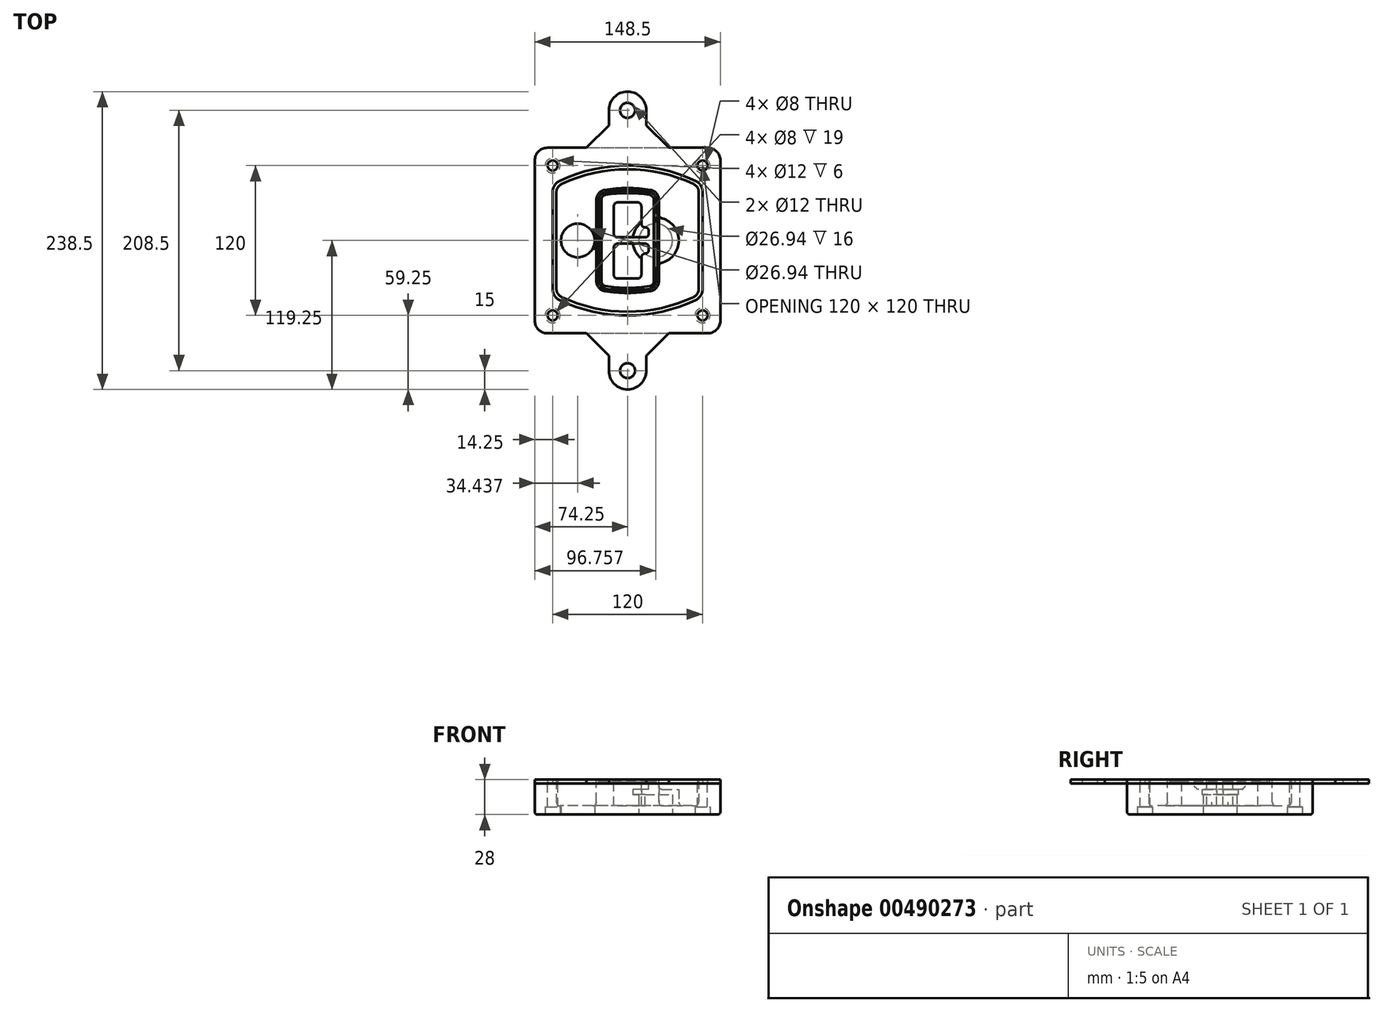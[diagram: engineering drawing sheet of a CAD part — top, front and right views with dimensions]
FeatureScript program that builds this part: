
annotation { "Feature Type Name" : "Feature", "Feature Type Description" : "" }
export const myFeature = defineFeature(function(context is Context, id is Id, definition is map)
    precondition{}
    {
        {
            var Q0;
            Q0=qCreatedBy(makeId("Top.planeOp"),FACE);
            var sketch = newSketch(context, id + "F0", { "sketchPlane" : qUnion([Q0])});
            skPoint(sketch, "E0.rect.middle", {"position": v(0, 0) * mm});
            skLineSegment(sketch, "E1.bottom", {"start": v(-64.25, -74.25) * mm, "end": v(64.25, -74.25) * mm});
            skLineSegment(sketch, "E1.top", {"start": v(-64.25, 74.25) * mm, "end": v(64.25, 74.25) * mm});
            skLineSegment(sketch, "E1.left", {"start": v(-74.25, -64.25) * mm, "end": v(-74.25, 64.25) * mm});
            skLineSegment(sketch, "E1.right", {"start": v(74.25, -64.25) * mm, "end": v(74.25, 64.25) * mm});
            skLineSegment(sketch, "E2", {"start": v(-74.25, 74.25) * mm, "end": v(74.25, -74.25) * mm, "construction": true});
            skLineSegment(sketch, "E3", {"start": v(74.25, 74.25) * mm, "end": v(-74.25, -74.25) * mm, "construction": true});
            skCircle(sketch, "E4", {"center": v(-60, 60) * mm, "radius": 4 * mm});
            skCircle(sketch, "E5", {"center": v(60, 60) * mm, "radius": 4 * mm});
            skCircle(sketch, "E6", {"center": v(60, -60) * mm, "radius": 4 * mm});
            skCircle(sketch, "E7", {"center": v(-60, -60) * mm, "radius": 4 * mm});
            skLineSegment(sketch, "E8", {"start": v(-60, 60) * mm, "end": v(60, 60) * mm, "construction": true});
            skLineSegment(sketch, "E9", {"start": v(60, 60) * mm, "end": v(60, -60) * mm, "construction": true});
            skLineSegment(sketch, "E10", {"start": v(60, -60) * mm, "end": v(-60, -60) * mm, "construction": true});
            skLineSegment(sketch, "E11", {"start": v(-60, -60) * mm, "end": v(-60, 60) * mm, "construction": true});
            skLineSegment(sketch, "E12", {"start": v(-60, 38.83) * mm, "end": v(-60, -38.83) * mm});
            skLineSegment(sketch, "E13", {"start": v(60, 38.83) * mm, "end": v(60, -38.83) * mm});
            skArc(sketch, "E14", {"start": v(54.26, 47.88) * mm, "mid": v(0, 60) * mm, "end": v(-54.26, 47.88) * mm});
            skArc(sketch, "E15", {"start": v(-54.26, -47.88) * mm, "mid": v(0, -60) * mm, "end": v(54.26, -47.88) * mm});
            skLineSegment(sketch, "E16", {"start": v(-60, 0) * mm, "end": v(60, 0) * mm, "construction": true});
            skPoint(sketch, "E17.visualSharp", {"position": v(-60, -45) * mm});
            skArc(sketch, "E17.filletArc", {"start": v(-60, -38.83) * mm, "mid": v(-58.44, -44.2) * mm, "end": v(-54.26, -47.88) * mm});
            skPoint(sketch, "E18.visualSharp", {"position": v(-60, 45) * mm});
            skArc(sketch, "E18.filletArc", {"start": v(-54.26, 47.88) * mm, "mid": v(-58.44, 44.2) * mm, "end": v(-60, 38.83) * mm});
            skPoint(sketch, "E19.visualSharp", {"position": v(60, 45) * mm});
            skArc(sketch, "E19.filletArc", {"start": v(60, 38.83) * mm, "mid": v(58.44, 44.2) * mm, "end": v(54.26, 47.88) * mm});
            skPoint(sketch, "E20.visualSharp", {"position": v(60, -45) * mm});
            skArc(sketch, "E20.filletArc", {"start": v(54.26, -47.88) * mm, "mid": v(58.44, -44.2) * mm, "end": v(60, -38.83) * mm});
            skPoint(sketch, "E21.visualSharp", {"position": v(-74.25, 74.25) * mm});
            skArc(sketch, "E21.filletArc", {"start": v(-64.25, 74.25) * mm, "mid": v(-71.32, 71.32) * mm, "end": v(-74.25, 64.25) * mm});
            skPoint(sketch, "E22.visualSharp", {"position": v(74.25, 74.25) * mm});
            skArc(sketch, "E22.filletArc", {"start": v(74.25, 64.25) * mm, "mid": v(71.32, 71.32) * mm, "end": v(64.25, 74.25) * mm});
            skPoint(sketch, "E23.visualSharp", {"position": v(74.25, -74.25) * mm});
            skArc(sketch, "E23.filletArc", {"start": v(64.25, -74.25) * mm, "mid": v(71.32, -71.32) * mm, "end": v(74.25, -64.25) * mm});
            skPoint(sketch, "E24.visualSharp", {"position": v(-74.25, -74.25) * mm});
            skArc(sketch, "E24.filletArc", {"start": v(-74.25, -64.25) * mm, "mid": v(-71.32, -71.32) * mm, "end": v(-64.25, -74.25) * mm});
            skArc(sketch, "E25.0", {"start": v(57, 38.83) * mm, "mid": v(55.9, 42.58) * mm, "end": v(52.98, 45.17) * mm});
            skLineSegment(sketch, "E25.1", {"start": v(57, 38.83) * mm, "end": v(57, -38.83) * mm});
            skArc(sketch, "E25.2", {"start": v(52.98, -45.17) * mm, "mid": v(55.9, -42.58) * mm, "end": v(57, -38.83) * mm});
            skArc(sketch, "E25.3", {"start": v(-52.98, -45.17) * mm, "mid": v(0, -57) * mm, "end": v(52.98, -45.17) * mm});
            skArc(sketch, "E25.4", {"start": v(-57, -38.83) * mm, "mid": v(-55.9, -42.58) * mm, "end": v(-52.98, -45.17) * mm});
            skArc(sketch, "E25.5", {"start": v(52.98, 45.17) * mm, "mid": v(0, 57) * mm, "end": v(-52.98, 45.17) * mm});
            skLineSegment(sketch, "E25.6", {"start": v(-57, 38.83) * mm, "end": v(-57, -38.83) * mm});
            skArc(sketch, "E25.7", {"start": v(-52.98, 45.17) * mm, "mid": v(-55.9, 42.58) * mm, "end": v(-57, 38.83) * mm});
            skArc(sketch, "E26.0", {"start": v(-55.96, 51.5) * mm, "mid": v(-61.82, 46.33) * mm, "end": v(-64, 38.83) * mm});
            skArc(sketch, "E26.1", {"start": v(55.96, 51.5) * mm, "mid": v(0, 64) * mm, "end": v(-55.96, 51.5) * mm});
            skArc(sketch, "E26.2", {"start": v(64, 38.83) * mm, "mid": v(61.82, 46.33) * mm, "end": v(55.96, 51.5) * mm});
            skLineSegment(sketch, "E26.3", {"start": v(64, 38.83) * mm, "end": v(64, -38.83) * mm});
            skArc(sketch, "E26.4", {"start": v(55.96, -51.5) * mm, "mid": v(61.82, -46.33) * mm, "end": v(64, -38.83) * mm});
            skLineSegment(sketch, "E26.5", {"start": v(-64, 38.83) * mm, "end": v(-64, -38.83) * mm});
            skArc(sketch, "E26.6", {"start": v(-55.96, -51.5) * mm, "mid": v(0, -64) * mm, "end": v(55.96, -51.5) * mm});
            skArc(sketch, "E26.7", {"start": v(-64, -38.83) * mm, "mid": v(-61.82, -46.33) * mm, "end": v(-55.96, -51.5) * mm});
            skSolve(sketch);
        }
        {
            var Q0;
            Q0=makeQuery(id+"F0.imprint","IMPRINT",FACE,{"disambiguationData":[TD([[makeQuery(id+"F0.imprint","IMPRINT",EDGE,{"derivedFrom":sQuery(id+"F0.wireOp",EDGE,"E1.bottom")}),1.0]])]});
            var Q1;
            Q1=makeQuery(id+"F0.imprint","IMPRINT",FACE,{"disambiguationData":[TD([[makeQuery(id+"F0.imprint","IMPRINT",EDGE,{"derivedFrom":sQuery(id+"F0.wireOp",EDGE,"E12")}),1.0]])]});
            var Q2;
            Q2=makeQuery(id+"F0.imprint","IMPRINT",FACE,{"disambiguationData":[TD([[makeQuery(id+"F0.imprint","IMPRINT",EDGE,{"derivedFrom":sQuery(id+"F0.wireOp",EDGE,"E25.0")}),1.0]])]});
            var Q3;
            Q3=makeQuery(id+"F0.imprint","IMPRINT",FACE,{"disambiguationData":[TD([[makeQuery(id+"F0.imprint","IMPRINT",EDGE,{"derivedFrom":sQuery(id+"F0.wireOp",EDGE,"E12")}),-1.0]])]});
            extrude(context, id + "F1", {"entities" : qUnion([Q0, Q1, Q2, Q3]), "oppositeDirection" : true, "depth" : 25 * mm});
        }
        {
            var Q0;
            Q0=makeQuery(id+"F0.imprint","IMPRINT",FACE,{"disambiguationData":[TD([[makeQuery(id+"F0.imprint","IMPRINT",EDGE,{"derivedFrom":sQuery(id+"F0.wireOp",EDGE,"E12")}),1.0]])]});
            extrude(context, id + "F2", {"entities" : qUnion([Q0]), "operationType" : NewBodyOperationType.ADD, "depth" : 3 * mm});
        }
        {
            var Q0;
            Q0=makeQuery(id+"F0.imprint","IMPRINT",FACE,{"disambiguationData":[TD([[makeQuery(id+"F0.imprint","IMPRINT",EDGE,{"derivedFrom":sQuery(id+"F0.wireOp",EDGE,"E25.0")}),1.0]])]});
            extrude(context, id + "F3", {"entities" : qUnion([Q0]), "operationType" : NewBodyOperationType.REMOVE, "oppositeDirection" : true, "depth" : 18 * mm});
        }
        {
            var Q0;
            Q0=makeQuery(id+"F2.opExtrude","CAP_FACE",FACE,{"disambiguationData":[OSD([sQuery(id+"F0.wireOp",EDGE,"E12"),sQuery(id+"F0.wireOp",EDGE,"E13"),sQuery(id+"F0.wireOp",EDGE,"E14"),sQuery(id+"F0.wireOp",EDGE,"E15"),sQuery(id+"F0.wireOp",EDGE,"E17.filletArc"),sQuery(id+"F0.wireOp",EDGE,"E18.filletArc"),sQuery(id+"F0.wireOp",EDGE,"E19.filletArc"),sQuery(id+"F0.wireOp",EDGE,"E20.filletArc"),sQuery(id+"F0.wireOp",EDGE,"E25.0"),sQuery(id+"F0.wireOp",EDGE,"E25.1"),sQuery(id+"F0.wireOp",EDGE,"E25.2"),sQuery(id+"F0.wireOp",EDGE,"E25.3"),sQuery(id+"F0.wireOp",EDGE,"E25.4"),sQuery(id+"F0.wireOp",EDGE,"E25.5"),sQuery(id+"F0.wireOp",EDGE,"E25.6"),sQuery(id+"F0.wireOp",EDGE,"E25.7")])],"isStart":false});
            var sketch = newSketch(context, id + "F4", { "sketchPlane" : qUnion([Q0])});
            skArc(sketch, "E27.0", {"start": v(-18.34, -40.45) * mm, "mid": v(0, -42) * mm, "end": v(18.34, -40.45) * mm});
            skArc(sketch, "E28.0", {"start": v(18.34, 40.45) * mm, "mid": v(0, 42) * mm, "end": v(-18.34, 40.45) * mm});
            skLineSegment(sketch, "E29", {"start": v(-25, 32.57) * mm, "end": v(-25, -32.57) * mm});
            skLineSegment(sketch, "E30", {"start": v(25, 32.57) * mm, "end": v(25, -32.57) * mm});
            skLineSegment(sketch, "E31", {"start": v(-25, 39.1) * mm, "end": v(25, 39.1) * mm, "construction": true});
            skLineSegment(sketch, "E32", {"start": v(-25, -39.1) * mm, "end": v(25, -39.1) * mm, "construction": true});
            skPoint(sketch, "E33.visualSharp", {"position": v(-25, 39.1) * mm});
            skArc(sketch, "E33.filletArc", {"start": v(-18.34, 40.45) * mm, "mid": v(-23.11, 37.73) * mm, "end": v(-25, 32.57) * mm});
            skPoint(sketch, "E34.visualSharp", {"position": v(25, 39.1) * mm});
            skArc(sketch, "E34.filletArc", {"start": v(25, 32.57) * mm, "mid": v(23.11, 37.73) * mm, "end": v(18.34, 40.45) * mm});
            skPoint(sketch, "E35.visualSharp", {"position": v(25, -39.1) * mm});
            skArc(sketch, "E35.filletArc", {"start": v(18.34, -40.45) * mm, "mid": v(23.11, -37.73) * mm, "end": v(25, -32.57) * mm});
            skPoint(sketch, "E36.visualSharp", {"position": v(-25, -39.1) * mm});
            skArc(sketch, "E36.filletArc", {"start": v(-25, -32.57) * mm, "mid": v(-23.11, -37.73) * mm, "end": v(-18.34, -40.45) * mm});
            skArc(sketch, "E37.0", {"start": v(52.98, 45.17) * mm, "mid": v(0, 57) * mm, "end": v(-52.98, 45.17) * mm});
            skArc(sketch, "E37.1", {"start": v(-52.98, 45.17) * mm, "mid": v(-55.9, 42.58) * mm, "end": v(-57, 38.83) * mm});
            skLineSegment(sketch, "E37.2", {"start": v(-57, 38.83) * mm, "end": v(-57, -38.83) * mm});
            skArc(sketch, "E37.3", {"start": v(-57, -38.83) * mm, "mid": v(-55.9, -42.58) * mm, "end": v(-52.98, -45.17) * mm});
            skArc(sketch, "E37.4", {"start": v(-52.98, -45.17) * mm, "mid": v(0, -57) * mm, "end": v(52.98, -45.17) * mm});
            skArc(sketch, "E37.5", {"start": v(52.98, -45.17) * mm, "mid": v(55.9, -42.58) * mm, "end": v(57, -38.83) * mm});
            skLineSegment(sketch, "E37.6", {"start": v(57, 38.83) * mm, "end": v(57, -38.83) * mm});
            skArc(sketch, "E37.7", {"start": v(57, 38.83) * mm, "mid": v(55.9, 42.58) * mm, "end": v(52.98, 45.17) * mm});
            skLineSegment(sketch, "E38.0", {"start": v(23, 32.57) * mm, "end": v(23, -32.57) * mm});
            skArc(sketch, "E38.1", {"start": v(18, -38.48) * mm, "mid": v(21.58, -36.44) * mm, "end": v(23, -32.57) * mm});
            skArc(sketch, "E38.2", {"start": v(-18, -38.48) * mm, "mid": v(0, -40) * mm, "end": v(18, -38.48) * mm});
            skArc(sketch, "E38.3", {"start": v(-23, -32.57) * mm, "mid": v(-21.58, -36.44) * mm, "end": v(-18, -38.48) * mm});
            skLineSegment(sketch, "E38.4", {"start": v(-23, 32.57) * mm, "end": v(-23, -32.57) * mm});
            skArc(sketch, "E38.5", {"start": v(23, 32.57) * mm, "mid": v(21.58, 36.44) * mm, "end": v(18, 38.48) * mm});
            skArc(sketch, "E38.6", {"start": v(-18, 38.48) * mm, "mid": v(-21.58, 36.44) * mm, "end": v(-23, 32.57) * mm});
            skArc(sketch, "E38.7", {"start": v(18, 38.48) * mm, "mid": v(0, 40) * mm, "end": v(-18, 38.48) * mm});
            skArc(sketch, "E39.0", {"start": v(21, 32.57) * mm, "mid": v(20.06, 35.15) * mm, "end": v(17.67, 36.5) * mm});
            skLineSegment(sketch, "E39.1", {"start": v(21, 32.57) * mm, "end": v(21, -32.57) * mm});
            skArc(sketch, "E39.2", {"start": v(17.67, -36.5) * mm, "mid": v(20.06, -35.15) * mm, "end": v(21, -32.57) * mm});
            skArc(sketch, "E39.3", {"start": v(-17.67, -36.5) * mm, "mid": v(0, -38) * mm, "end": v(17.67, -36.5) * mm});
            skArc(sketch, "E39.4", {"start": v(-21, -32.57) * mm, "mid": v(-20.06, -35.15) * mm, "end": v(-17.67, -36.5) * mm});
            skArc(sketch, "E39.5", {"start": v(17.67, 36.5) * mm, "mid": v(0, 38) * mm, "end": v(-17.67, 36.5) * mm});
            skLineSegment(sketch, "E39.6", {"start": v(-21, 32.57) * mm, "end": v(-21, -32.57) * mm});
            skArc(sketch, "E39.7", {"start": v(-17.67, 36.5) * mm, "mid": v(-20.06, 35.15) * mm, "end": v(-21, 32.57) * mm});
            skLineSegment(sketch, "E40", {"start": v(-25, 0) * mm, "end": v(25, 0) * mm, "construction": true});
            skLineSegment(sketch, "E41", {"start": v(-11, 5.5) * mm, "end": v(-11, 27.5) * mm});
            skLineSegment(sketch, "E42", {"start": v(-8, 30.5) * mm, "end": v(8, 30.5) * mm});
            skLineSegment(sketch, "E43", {"start": v(11, 27.5) * mm, "end": v(11, 13.5) * mm});
            skLineSegment(sketch, "E44", {"start": v(14, 10.5) * mm, "end": v(14, 10.5) * mm});
            skLineSegment(sketch, "E45", {"start": v(17, 7.5) * mm, "end": v(17, 5.5) * mm});
            skLineSegment(sketch, "E46", {"start": v(14, 2.5) * mm, "end": v(-8, 2.5) * mm});
            skPoint(sketch, "E47.visualSharp", {"position": v(-11, 30.5) * mm});
            skArc(sketch, "E47.filletArc", {"start": v(-8, 30.5) * mm, "mid": v(-10.12, 29.62) * mm, "end": v(-11, 27.5) * mm});
            skPoint(sketch, "E48.visualSharp", {"position": v(11, 30.5) * mm});
            skArc(sketch, "E48.filletArc", {"start": v(11, 27.5) * mm, "mid": v(10.12, 29.62) * mm, "end": v(8, 30.5) * mm});
            skPoint(sketch, "E49.visualSharp", {"position": v(11, 10.5) * mm});
            skArc(sketch, "E49.filletArc", {"start": v(11, 13.5) * mm, "mid": v(11.88, 11.38) * mm, "end": v(14, 10.5) * mm});
            skPoint(sketch, "E50.visualSharp", {"position": v(17, 10.5) * mm});
            skArc(sketch, "E50.filletArc", {"start": v(17, 7.5) * mm, "mid": v(16.12, 9.62) * mm, "end": v(14, 10.5) * mm});
            skPoint(sketch, "E51.visualSharp", {"position": v(17, 2.5) * mm});
            skArc(sketch, "E51.filletArc", {"start": v(14, 2.5) * mm, "mid": v(16.12, 3.38) * mm, "end": v(17, 5.5) * mm});
            skPoint(sketch, "E52.visualSharp", {"position": v(-11, 2.5) * mm});
            skArc(sketch, "E52.filletArc", {"start": v(-11, 5.5) * mm, "mid": v(-10.12, 3.38) * mm, "end": v(-8, 2.5) * mm});
            skLineSegment(sketch, "E53.0.MirrorCS", {"start": v(14, -2.5) * mm, "end": v(-8, -2.5) * mm});
            skArc(sketch, "E54.0.MirrorCS", {"start": v(-11, -5.5) * mm, "mid": v(-10.12, -3.38) * mm, "end": v(-8, -2.5) * mm});
            skLineSegment(sketch, "E55.0.MirrorCS", {"start": v(-11, -5.5) * mm, "end": v(-11, -27.5) * mm});
            skArc(sketch, "E56.0.MirrorCS", {"start": v(-8, -30.5) * mm, "mid": v(-10.12, -29.62) * mm, "end": v(-11, -27.5) * mm});
            skLineSegment(sketch, "E57.0.MirrorCS", {"start": v(-8, -30.5) * mm, "end": v(8, -30.5) * mm});
            skArc(sketch, "E58.0.MirrorCS", {"start": v(11, -27.5) * mm, "mid": v(10.12, -29.62) * mm, "end": v(8, -30.5) * mm});
            skLineSegment(sketch, "E59.0.MirrorCS", {"start": v(11, -27.5) * mm, "end": v(11, -13.5) * mm});
            skArc(sketch, "E60.0.MirrorCS", {"start": v(11, -13.5) * mm, "mid": v(11.88, -11.38) * mm, "end": v(14, -10.5) * mm});
            skArc(sketch, "E61.0.MirrorCS", {"start": v(17, -7.5) * mm, "mid": v(16.12, -9.62) * mm, "end": v(14, -10.5) * mm});
            skLineSegment(sketch, "E62.0.MirrorCS", {"start": v(17, -7.5) * mm, "end": v(17, -5.5) * mm});
            skArc(sketch, "E63.0.MirrorCS", {"start": v(14, -2.5) * mm, "mid": v(16.12, -3.38) * mm, "end": v(17, -5.5) * mm});
            skSolve(sketch);
        }
        {
            var Q0;
            Q0=makeQuery(id+"F4.imprint","IMPRINT",FACE,{"disambiguationData":[TD([[makeQuery(id+"F4.imprint","IMPRINT",EDGE,{"derivedFrom":sQuery(id+"F4.wireOp",EDGE,"E27.0")}),1.0]])]});
            var Q1;
            Q1=makeQuery(id+"F4.imprint","IMPRINT",FACE,{"disambiguationData":[TD([[makeQuery(id+"F4.imprint","IMPRINT",EDGE,{"derivedFrom":sQuery(id+"F4.wireOp",EDGE,"E38.0")}),-1.0]])]});
            var Q2;
            Q2=makeQuery(id+"F4.imprint","IMPRINT",FACE,{"disambiguationData":[TD([[makeQuery(id+"F4.imprint","IMPRINT",EDGE,{"derivedFrom":sQuery(id+"F4.wireOp",EDGE,"E39.0")}),1.0]])]});
            extrude(context, id + "F5", {"entities" : qUnion([Q0, Q1, Q2]), "operationType" : NewBodyOperationType.ADD, "endBound" : BoundingType.UP_TO_NEXT, "oppositeDirection" : true, "depth" : 25 * mm});
        }
        {
            var Q0;
            Q0=makeQuery(id+"F4.imprint","IMPRINT",FACE,{"disambiguationData":[TD([[makeQuery(id+"F4.imprint","IMPRINT",EDGE,{"derivedFrom":sQuery(id+"F4.wireOp",EDGE,"E38.0")}),-1.0]])]});
            extrude(context, id + "F6", {"entities" : qUnion([Q0]), "operationType" : NewBodyOperationType.REMOVE, "oppositeDirection" : true, "depth" : 2 * mm});
        }
        {
            var Q0;
            Q0=makeQuery(id+"F1.opExtrude","CAP_FACE",FACE,{"disambiguationData":[OSD([sQuery(id+"F0.wireOp",EDGE,"E1.bottom"),sQuery(id+"F0.wireOp",EDGE,"E1.top"),sQuery(id+"F0.wireOp",EDGE,"E1.left"),sQuery(id+"F0.wireOp",EDGE,"E1.right"),sQuery(id+"F0.wireOp",EDGE,"E4"),sQuery(id+"F0.wireOp",EDGE,"E5"),sQuery(id+"F0.wireOp",EDGE,"E6"),sQuery(id+"F0.wireOp",EDGE,"E7"),sQuery(id+"F0.wireOp",EDGE,"E21.filletArc"),sQuery(id+"F0.wireOp",EDGE,"E22.filletArc"),sQuery(id+"F0.wireOp",EDGE,"E23.filletArc"),sQuery(id+"F0.wireOp",EDGE,"E24.filletArc")])],"isStart":false});
            var sketch = newSketch(context, id + "F7", { "sketchPlane" : qUnion([Q0])});
            skCircle(sketch, "E64", {"center": v(22.5, 0) * mm, "radius": 13.47 * mm});
            skCircle(sketch, "E65", {"center": v(-39.81, 0) * mm, "radius": 13.47 * mm});
            skLineSegment(sketch, "E66", {"start": v(74.25, 0) * mm, "end": v(-74.25, 0) * mm});
            skCircle(sketch, "E67", {"center": v(22.5, 0) * mm, "radius": 18.47 * mm});
            skCircle(sketch, "E68", {"center": v(60, -60) * mm, "radius": 6 * mm});
            skCircle(sketch, "E69", {"center": v(-60, -60) * mm, "radius": 6 * mm});
            skCircle(sketch, "E70", {"center": v(-60, 60) * mm, "radius": 6 * mm});
            skCircle(sketch, "E71", {"center": v(60, 60) * mm, "radius": 6 * mm});
            skSolve(sketch);
        }
        {
            var Q0;
            {var subQ1=sQuery(id+"F7.wireOp",EDGE,"E66");var subQ4=sQuery(id+"F7.wireOp",EDGE,"E64");var subQ6=makeQuery(id+"F7.imprint","INTERSECT",VERTEX,{"disambiguationData":[OD(0.0)],"derivedFrom":[subQ4,subQ1]});Q0=makeQuery(id+"F7.imprint","IMPRINT",FACE,{"disambiguationData":[TD([[makeQuery(id+"F7.imprint","IMPRINT",EDGE,{"disambiguationData":[TD([[subQ6,-1.0]])],"derivedFrom":subQ4}),-1.0]])]});}
            var Q1;
            {var subQ0=sQuery(id+"F7.wireOp",EDGE,"E66");var subQ1=sQuery(id+"F7.wireOp",EDGE,"E64");var subQ3=makeQuery(id+"F7.imprint","INTERSECT",VERTEX,{"disambiguationData":[OD(0.0)],"derivedFrom":[subQ1,subQ0]});Q1=makeQuery(id+"F7.imprint","IMPRINT",FACE,{"disambiguationData":[TD([[makeQuery(id+"F7.imprint","IMPRINT",EDGE,{"disambiguationData":[TD([[subQ3,-1.0]])],"derivedFrom":subQ1}),1.0]])]});}
            var Q2;
            {var subQ0=sQuery(id+"F7.wireOp",EDGE,"E66");var subQ1=sQuery(id+"F7.wireOp",EDGE,"E64");var subQ3=makeQuery(id+"F7.imprint","INTERSECT",VERTEX,{"disambiguationData":[OD(0.0)],"derivedFrom":[subQ1,subQ0]});Q2=makeQuery(id+"F7.imprint","IMPRINT",FACE,{"disambiguationData":[TD([[makeQuery(id+"F7.imprint","IMPRINT",EDGE,{"disambiguationData":[TD([[subQ3,1.0]])],"derivedFrom":subQ1}),1.0]])]});}
            var Q3;
            {var subQ1=sQuery(id+"F7.wireOp",EDGE,"E66");var subQ4=sQuery(id+"F7.wireOp",EDGE,"E64");var subQ6=makeQuery(id+"F7.imprint","INTERSECT",VERTEX,{"disambiguationData":[OD(0.0)],"derivedFrom":[subQ4,subQ1]});Q3=makeQuery(id+"F7.imprint","IMPRINT",FACE,{"disambiguationData":[TD([[makeQuery(id+"F7.imprint","IMPRINT",EDGE,{"disambiguationData":[TD([[subQ6,1.0]])],"derivedFrom":subQ4}),-1.0]])]});}
            extrude(context, id + "F8", {"entities" : qUnion([Q0, Q1, Q2, Q3]), "operationType" : NewBodyOperationType.ADD, "oppositeDirection" : true, "depth" : 20 * mm});
        }
        {
            var Q0;
            {var subQ0=sQuery(id+"F7.wireOp",EDGE,"E66");var subQ1=sQuery(id+"F7.wireOp",EDGE,"E64");var subQ3=makeQuery(id+"F7.imprint","INTERSECT",VERTEX,{"disambiguationData":[OD(0.0)],"derivedFrom":[subQ1,subQ0]});Q0=makeQuery(id+"F7.imprint","IMPRINT",FACE,{"disambiguationData":[TD([[makeQuery(id+"F7.imprint","IMPRINT",EDGE,{"disambiguationData":[TD([[subQ3,-1.0]])],"derivedFrom":subQ1}),1.0]])]});}
            var Q1;
            {var subQ0=sQuery(id+"F7.wireOp",EDGE,"E66");var subQ1=sQuery(id+"F7.wireOp",EDGE,"E64");var subQ3=makeQuery(id+"F7.imprint","INTERSECT",VERTEX,{"disambiguationData":[OD(0.0)],"derivedFrom":[subQ1,subQ0]});Q1=makeQuery(id+"F7.imprint","IMPRINT",FACE,{"disambiguationData":[TD([[makeQuery(id+"F7.imprint","IMPRINT",EDGE,{"disambiguationData":[TD([[subQ3,1.0]])],"derivedFrom":subQ1}),1.0]])]});}
            extrude(context, id + "F9", {"entities" : qUnion([Q0, Q1]), "operationType" : NewBodyOperationType.REMOVE, "oppositeDirection" : true, "depth" : 16 * mm});
        }
        {
            var Q0;
            {var subQ0=sQuery(id+"F7.wireOp",EDGE,"E66");var subQ1=sQuery(id+"F7.wireOp",EDGE,"E65");var subQ3=makeQuery(id+"F7.imprint","INTERSECT",VERTEX,{"disambiguationData":[OD(0.0)],"derivedFrom":[subQ1,subQ0]});Q0=makeQuery(id+"F7.imprint","IMPRINT",FACE,{"disambiguationData":[TD([[makeQuery(id+"F7.imprint","IMPRINT",EDGE,{"disambiguationData":[TD([[subQ3,-1.0]])],"derivedFrom":subQ1}),1.0]])]});}
            var Q1;
            {var subQ0=sQuery(id+"F7.wireOp",EDGE,"E66");var subQ1=sQuery(id+"F7.wireOp",EDGE,"E65");var subQ3=makeQuery(id+"F7.imprint","INTERSECT",VERTEX,{"disambiguationData":[OD(0.0)],"derivedFrom":[subQ1,subQ0]});Q1=makeQuery(id+"F7.imprint","IMPRINT",FACE,{"disambiguationData":[TD([[makeQuery(id+"F7.imprint","IMPRINT",EDGE,{"disambiguationData":[TD([[subQ3,1.0]])],"derivedFrom":subQ1}),1.0]])]});}
            extrude(context, id + "F10", {"entities" : qUnion([Q0, Q1]), "operationType" : NewBodyOperationType.REMOVE, "oppositeDirection" : true, "depth" : 25 * mm});
        }
        {
            var Q0;
            Q0=makeQuery(id+"F7.imprint","IMPRINT",FACE,{"disambiguationData":[TD([[makeQuery(id+"F7.imprint","IMPRINT",EDGE,{"derivedFrom":sQuery(id+"F7.wireOp",EDGE,"E68")}),1.0]])]});
            var Q1;
            Q1=makeQuery(id+"F7.imprint","IMPRINT",FACE,{"disambiguationData":[TD([[makeQuery(id+"F7.imprint","IMPRINT",EDGE,{"derivedFrom":makeQuery(id+"F1.opExtrude","CAP_EDGE",EDGE,{"disambiguationData":[OSD([sQuery(id+"F0.wireOp",EDGE,"E5")])],"isStart":false})}),-1.0]])]});
            var Q2;
            Q2=makeQuery(id+"F7.imprint","IMPRINT",FACE,{"disambiguationData":[TD([[makeQuery(id+"F7.imprint","IMPRINT",EDGE,{"derivedFrom":sQuery(id+"F7.wireOp",EDGE,"E69")}),1.0]])]});
            var Q3;
            Q3=makeQuery(id+"F7.imprint","IMPRINT",FACE,{"disambiguationData":[TD([[makeQuery(id+"F7.imprint","IMPRINT",EDGE,{"derivedFrom":makeQuery(id+"F1.opExtrude","CAP_EDGE",EDGE,{"disambiguationData":[OSD([sQuery(id+"F0.wireOp",EDGE,"E4")])],"isStart":false})}),-1.0]])]});
            var Q4;
            Q4=makeQuery(id+"F7.imprint","IMPRINT",FACE,{"disambiguationData":[TD([[makeQuery(id+"F7.imprint","IMPRINT",EDGE,{"derivedFrom":sQuery(id+"F7.wireOp",EDGE,"E70")}),1.0]])]});
            var Q5;
            Q5=makeQuery(id+"F7.imprint","IMPRINT",FACE,{"disambiguationData":[TD([[makeQuery(id+"F7.imprint","IMPRINT",EDGE,{"derivedFrom":makeQuery(id+"F1.opExtrude","CAP_EDGE",EDGE,{"disambiguationData":[OSD([sQuery(id+"F0.wireOp",EDGE,"E7")])],"isStart":false})}),-1.0]])]});
            var Q6;
            Q6=makeQuery(id+"F7.imprint","IMPRINT",FACE,{"disambiguationData":[TD([[makeQuery(id+"F7.imprint","IMPRINT",EDGE,{"derivedFrom":sQuery(id+"F7.wireOp",EDGE,"E71")}),1.0]])]});
            var Q7;
            Q7=makeQuery(id+"F7.imprint","IMPRINT",FACE,{"disambiguationData":[TD([[makeQuery(id+"F7.imprint","IMPRINT",EDGE,{"derivedFrom":makeQuery(id+"F1.opExtrude","CAP_EDGE",EDGE,{"disambiguationData":[OSD([sQuery(id+"F0.wireOp",EDGE,"E6")])],"isStart":false})}),-1.0]])]});
            extrude(context, id + "F11", {"entities" : qUnion([Q0, Q1, Q2, Q3, Q4, Q5, Q6, Q7]), "operationType" : NewBodyOperationType.REMOVE, "oppositeDirection" : true, "depth" : 6 * mm});
        }
        {
            var Q0;
            Q0=makeQuery(id+"F9.boolean.opBoolean","COPY",FACE,{"derivedFrom":makeQuery(id+"F9.opExtrude","CAP_FACE",FACE,{"disambiguationData":[OSD([sQuery(id+"F7.wireOp",EDGE,"E64")])],"isStart":false})});
            var sketch = newSketch(context, id + "F12", { "sketchPlane" : qUnion([Q0])});
            skArc(sketch, "E72.0", {"start": v(11, 14.45) * mm, "mid": v(6.45, 9.13) * mm, "end": v(4.2, 2.5) * mm});
            skArc(sketch, "E72.1", {"start": v(4.2, -2.5) * mm, "mid": v(6.45, -9.13) * mm, "end": v(11, -14.45) * mm});
            skLineSegment(sketch, "E73", {"start": v(4.2, -2.5) * mm, "end": v(14, -2.5) * mm});
            skLineSegment(sketch, "E74.0", {"start": v(14, 2.5) * mm, "end": v(4.2, 2.5) * mm});
            skArc(sketch, "E74.1", {"start": v(14, 2.5) * mm, "mid": v(16.12, 3.38) * mm, "end": v(17, 5.5) * mm});
            skLineSegment(sketch, "E74.2", {"start": v(17, 7.5) * mm, "end": v(17, 5.5) * mm});
            skArc(sketch, "E74.3", {"start": v(17, 7.5) * mm, "mid": v(16.12, 9.62) * mm, "end": v(14, 10.5) * mm});
            skArc(sketch, "E74.4", {"start": v(11, 13.5) * mm, "mid": v(11.88, 11.38) * mm, "end": v(14, 10.5) * mm});
            skLineSegment(sketch, "E74.5", {"start": v(11, 14.45) * mm, "end": v(11, 13.5) * mm});
            skLineSegment(sketch, "E74.7", {"start": v(14, -2.5) * mm, "end": v(4.2, -2.5) * mm});
            skArc(sketch, "E74.8", {"start": v(14, -2.5) * mm, "mid": v(16.12, -3.38) * mm, "end": v(17, -5.5) * mm});
            skLineSegment(sketch, "E74.9", {"start": v(17, -7.5) * mm, "end": v(17, -5.5) * mm});
            skArc(sketch, "E74.10", {"start": v(17, -7.5) * mm, "mid": v(16.12, -9.62) * mm, "end": v(14, -10.5) * mm});
            skArc(sketch, "E74.11", {"start": v(11, -13.5) * mm, "mid": v(11.88, -11.38) * mm, "end": v(14, -10.5) * mm});
            skLineSegment(sketch, "E74.12", {"start": v(11, -14.45) * mm, "end": v(11, -13.5) * mm});
            skPoint(sketch, "E75.orphan", {"position": v(11, -27.5) * mm});
            skPoint(sketch, "E76.orphan", {"position": v(-8, -2.5) * mm});
            skPoint(sketch, "E77.orphan", {"position": v(-8, 2.5) * mm});
            skPoint(sketch, "E78.orphan", {"position": v(11, 27.5) * mm});
            skSolve(sketch);
        }
        {
            var Q0;
            {var subQ7=sQuery(id+"F12.wireOp",EDGE,"E72.0");var subQ14=sQuery(id+"F12.wireOp",EDGE,"E72.1");var subQ16=sQuery(id+"F12.wireOp",EDGE,"E74.1");var subQ18=sQuery(id+"F12.wireOp",EDGE,"E74.8");Q0=qUnion([makeQuery(id+"F12.imprint","IMPRINT",FACE,{"disambiguationData":[TD([[makeQuery(id+"F12.imprint","IMPRINT",EDGE,{"derivedFrom":subQ7}),1.0]])]}),makeQuery(id+"F12.imprint","IMPRINT",FACE,{"disambiguationData":[TD([[makeQuery(id+"F12.imprint","IMPRINT",EDGE,{"derivedFrom":subQ14}),1.0]])]}),makeQuery(id+"F12.imprint","IMPRINT",FACE,{"disambiguationData":[TD([[makeQuery(id+"F12.imprint","IMPRINT",EDGE,{"derivedFrom":subQ16}),1.0]])]}),makeQuery(id+"F12.imprint","IMPRINT",FACE,{"disambiguationData":[TD([[makeQuery(id+"F12.imprint","IMPRINT",EDGE,{"derivedFrom":subQ18}),-1.0]])]})]);}
            var Q1;
            Q1=makeQuery(id+"F5.boolean.opBoolean","SPLIT",FACE,{"disambiguationData":[TD([makeQuery(id+"F5.opExtrude","SWEPT_FACE",FACE,{"disambiguationData":[OSD([sQuery(id+"F4.wireOp",EDGE,"E41")])]})])],"derivedFrom":makeQuery(id+"F3.boolean.opBoolean","COPY",FACE,{"derivedFrom":makeQuery(id+"F3.opExtrude","CAP_FACE",FACE,{"disambiguationData":[OSD([sQuery(id+"F0.wireOp",EDGE,"E25.0"),sQuery(id+"F0.wireOp",EDGE,"E25.1"),sQuery(id+"F0.wireOp",EDGE,"E25.2"),sQuery(id+"F0.wireOp",EDGE,"E25.3"),sQuery(id+"F0.wireOp",EDGE,"E25.4"),sQuery(id+"F0.wireOp",EDGE,"E25.5"),sQuery(id+"F0.wireOp",EDGE,"E25.6"),sQuery(id+"F0.wireOp",EDGE,"E25.7")])],"isStart":false})})});
            extrude(context, id + "F13", {"entities" : qUnion([Q0]), "operationType" : NewBodyOperationType.REMOVE, "endBound" : BoundingType.UP_TO_SURFACE, "endBoundEntityFace" : qUnion([Q1]), "depth" : 25 * mm});
        }
        {
            var Q0;
            Q0=makeQuery(id+"F3.boolean.opBoolean","COPY",EDGE,{"derivedFrom":makeQuery(id+"F3.opExtrude","CAP_EDGE",EDGE,{"disambiguationData":[OSD([sQuery(id+"F0.wireOp",EDGE,"E25.6")])],"isStart":false})});
            var Q1;
            Q1=makeQuery(id+"F8.boolean.opBoolean","INTERSECT",EDGE,{"derivedFrom":[makeQuery(id+"F5.opExtrude","SWEPT_FACE",FACE,{"disambiguationData":[OSD([sQuery(id+"F4.wireOp",EDGE,"E30")])]}),makeQuery(id+"F8.opExtrude","CAP_FACE",FACE,{"disambiguationData":[OSD([sQuery(id+"F7.wireOp",EDGE,"E67")])],"isStart":false})]});
            var Q2;
            Q2=makeQuery(id+"F8.boolean.opBoolean","INTERSECT",EDGE,{"disambiguationData":[OD(1.0)],"derivedFrom":[makeQuery(id+"F5.opExtrude","SWEPT_FACE",FACE,{"disambiguationData":[OSD([sQuery(id+"F4.wireOp",EDGE,"E30")])]}),makeQuery(id+"F8.opExtrude","SWEPT_FACE",FACE,{"disambiguationData":[OSD([sQuery(id+"F7.wireOp",EDGE,"E67")])]})]});
            var Q3;
            {var subQ0=sQuery(id+"F4.wireOp",EDGE,"E30");Q3=makeQuery(id+"F8.boolean.opBoolean","SPLIT",EDGE,{"disambiguationData":[TD([makeQuery(id+"F5.opExtrude","SWEPT_FACE",FACE,{"disambiguationData":[OSD([sQuery(id+"F4.wireOp",EDGE,"E35.filletArc")])]})])],"derivedFrom":makeQuery(id+"F5.opExtrude","CAP_EDGE",EDGE,{"disambiguationData":[OSD([subQ0])],"isStart":false})});}
            var Q4;
            {var subQ0=sQuery(id+"F0.wireOp",EDGE,"E25.7");var subQ1=sQuery(id+"F0.wireOp",EDGE,"E25.1");var subQ2=sQuery(id+"F0.wireOp",EDGE,"E25.6");var subQ3=sQuery(id+"F0.wireOp",EDGE,"E25.5");var subQ4=sQuery(id+"F0.wireOp",EDGE,"E25.4");var subQ5=sQuery(id+"F0.wireOp",EDGE,"E25.0");var subQ6=sQuery(id+"F0.wireOp",EDGE,"E25.2");var subQ7=sQuery(id+"F0.wireOp",EDGE,"E25.3");Q4=makeQuery(id+"F8.boolean.opBoolean","INTERSECT",EDGE,{"derivedFrom":[makeQuery(id+"F5.boolean.opBoolean","SPLIT",FACE,{"disambiguationData":[TD([makeQuery(id+"F2.opExtrude","SWEPT_FACE",FACE,{"disambiguationData":[OSD([subQ5])]})])],"derivedFrom":makeQuery(id+"F3.boolean.opBoolean","COPY",FACE,{"derivedFrom":makeQuery(id+"F3.opExtrude","CAP_FACE",FACE,{"disambiguationData":[OSD([subQ5,subQ1,subQ6,subQ7,subQ4,subQ3,subQ2,subQ0])],"isStart":false})})}),makeQuery(id+"F8.opExtrude","SWEPT_FACE",FACE,{"disambiguationData":[OSD([sQuery(id+"F7.wireOp",EDGE,"E67")])]})]});}
            var Q5;
            Q5=makeQuery(id+"F8.boolean.opBoolean","INTERSECT",EDGE,{"disambiguationData":[OD(0.0)],"derivedFrom":[makeQuery(id+"F5.opExtrude","SWEPT_FACE",FACE,{"disambiguationData":[OSD([sQuery(id+"F4.wireOp",EDGE,"E30")])]}),makeQuery(id+"F8.opExtrude","SWEPT_FACE",FACE,{"disambiguationData":[OSD([sQuery(id+"F7.wireOp",EDGE,"E67")])]})]});
            fillet(context, id + "F14", {"entities" : qUnion([Q0, Q1, Q2, Q3, Q4, Q5]), "radius" : 3 * mm, "tangentPropagation" : true, "allowEdgeOverflow" : false});
        }
        {
            var Q0;
            Q0=makeQuery(id+"F1.opExtrude","CAP_EDGE",EDGE,{"disambiguationData":[OSD([sQuery(id+"F0.wireOp",EDGE,"E1.bottom")])],"isStart":false});
            fillet(context, id + "F15", {"entities" : qUnion([Q0]), "radius" : 2 * mm, "tangentPropagation" : true, "allowEdgeOverflow" : false});
        }
        {
            var Q0;
            {var subQ0=sQuery(id+"F0.wireOp",EDGE,"E21.filletArc");var subQ1=sQuery(id+"F0.wireOp",EDGE,"E7");var subQ2=sQuery(id+"F0.wireOp",EDGE,"E6");var subQ3=sQuery(id+"F0.wireOp",EDGE,"E5");var subQ4=sQuery(id+"F0.wireOp",EDGE,"E4");var subQ5=sQuery(id+"F0.wireOp",EDGE,"E22.filletArc");var subQ6=sQuery(id+"F0.wireOp",EDGE,"E1.bottom");var subQ7=sQuery(id+"F0.wireOp",EDGE,"E1.right");var subQ8=sQuery(id+"F0.wireOp",EDGE,"E1.top");var subQ9=sQuery(id+"F0.wireOp",EDGE,"E1.left");var subQ10=sQuery(id+"F0.wireOp",EDGE,"E23.filletArc");var subQ11=sQuery(id+"F0.wireOp",EDGE,"E24.filletArc");Q0=makeQuery(id+"F2.boolean.opBoolean","SPLIT",FACE,{"disambiguationData":[TD([makeQuery(id+"F1.opExtrude","SWEPT_FACE",FACE,{"disambiguationData":[OSD([subQ6])]})])],"derivedFrom":makeQuery(id+"F1.opExtrude","CAP_FACE",FACE,{"disambiguationData":[OSD([subQ6,subQ8,subQ9,subQ7,subQ4,subQ3,subQ2,subQ1,subQ0,subQ5,subQ10,subQ11])],"isStart":true})});}
            var sketch = newSketch(context, id + "F16", { "sketchPlane" : qUnion([Q0])});
            skLineSegment(sketch, "E79", {"start": v(0, 74.25) * mm, "end": v(0, 104.25) * mm, "construction": true});
            skArc(sketch, "E80", {"start": v(15, 104.25) * mm, "mid": v(0, 119.25) * mm, "end": v(-15, 104.25) * mm});
            skLineSegment(sketch, "E81", {"start": v(15, 104.25) * mm, "end": v(15, 92.25) * mm});
            skLineSegment(sketch, "E82", {"start": v(-15, 104.25) * mm, "end": v(-15, 92.25) * mm});
            skLineSegment(sketch, "E83", {"start": v(15, 92.25) * mm, "end": v(33, 74.25) * mm});
            skLineSegment(sketch, "E84", {"start": v(-15, 92.25) * mm, "end": v(-33, 74.25) * mm});
            skCircle(sketch, "E85", {"center": v(0, 104.25) * mm, "radius": 6 * mm});
            skLineSegment(sketch, "E86", {"start": v(-74.25, 0) * mm, "end": v(74.25, 0) * mm, "construction": true});
            skLineSegment(sketch, "E87.MirrorCS", {"start": v(-15, -104.25) * mm, "end": v(-15, -92.25) * mm});
            skLineSegment(sketch, "E88.MirrorCS", {"start": v(15, -104.25) * mm, "end": v(15, -92.25) * mm});
            skCircle(sketch, "E89.MirrorC", {"center": v(0, -104.25) * mm, "radius": 6 * mm});
            skArc(sketch, "E90.MirrorCS", {"start": v(15, -104.25) * mm, "mid": v(0, -119.25) * mm, "end": v(-15, -104.25) * mm});
            skLineSegment(sketch, "E91.MirrorCS", {"start": v(0, -74.25) * mm, "end": v(0, -104.25) * mm, "construction": true});
            skLineSegment(sketch, "E92.MirrorCS", {"start": v(15, -92.25) * mm, "end": v(33, -74.25) * mm});
            skLineSegment(sketch, "E93.MirrorCS", {"start": v(-15, -92.25) * mm, "end": v(-33, -74.25) * mm});
            skSolve(sketch);
        }
        {
            var Q0;
            Q0=makeQuery(id+"F16.imprint","IMPRINT",FACE,{"disambiguationData":[TD([[makeQuery(id+"F16.imprint","IMPRINT",EDGE,{"derivedFrom":sQuery(id+"F16.wireOp",EDGE,"E80")}),1.0]])]});
            var Q1;
            Q1=makeQuery(id+"F16.imprint","IMPRINT",FACE,{"disambiguationData":[TD([[makeQuery(id+"F16.imprint","IMPRINT",EDGE,{"derivedFrom":sQuery(id+"F16.wireOp",EDGE,"E88.MirrorCS")}),1.0]])]});
            var Q2;
            Q2=makeQuery(id+"F16.imprint","IMPRINT",FACE,{"disambiguationData":[TD([[makeQuery(id+"F16.imprint","IMPRINT",EDGE,{"derivedFrom":makeQuery(id+"F1.opExtrude","CAP_EDGE",EDGE,{"disambiguationData":[OSD([sQuery(id+"F0.wireOp",EDGE,"E1.left")])],"isStart":true})}),-1.0]])]});
            var Q3;
            Q3=makeQuery(id+"F2.opExtrude","CAP_FACE",FACE,{"disambiguationData":[OSD([sQuery(id+"F0.wireOp",EDGE,"E12"),sQuery(id+"F0.wireOp",EDGE,"E13"),sQuery(id+"F0.wireOp",EDGE,"E14"),sQuery(id+"F0.wireOp",EDGE,"E15"),sQuery(id+"F0.wireOp",EDGE,"E17.filletArc"),sQuery(id+"F0.wireOp",EDGE,"E18.filletArc"),sQuery(id+"F0.wireOp",EDGE,"E19.filletArc"),sQuery(id+"F0.wireOp",EDGE,"E20.filletArc"),sQuery(id+"F0.wireOp",EDGE,"E25.0"),sQuery(id+"F0.wireOp",EDGE,"E25.1"),sQuery(id+"F0.wireOp",EDGE,"E25.2"),sQuery(id+"F0.wireOp",EDGE,"E25.3"),sQuery(id+"F0.wireOp",EDGE,"E25.4"),sQuery(id+"F0.wireOp",EDGE,"E25.5"),sQuery(id+"F0.wireOp",EDGE,"E25.6"),sQuery(id+"F0.wireOp",EDGE,"E25.7")])],"isStart":false});
            extrude(context, id + "F17", {"entities" : qUnion([Q0, Q1, Q2]), "endBound" : BoundingType.UP_TO_SURFACE, "endBoundEntityFace" : qUnion([Q3]), "depth" : 25 * mm});
        }
    });
